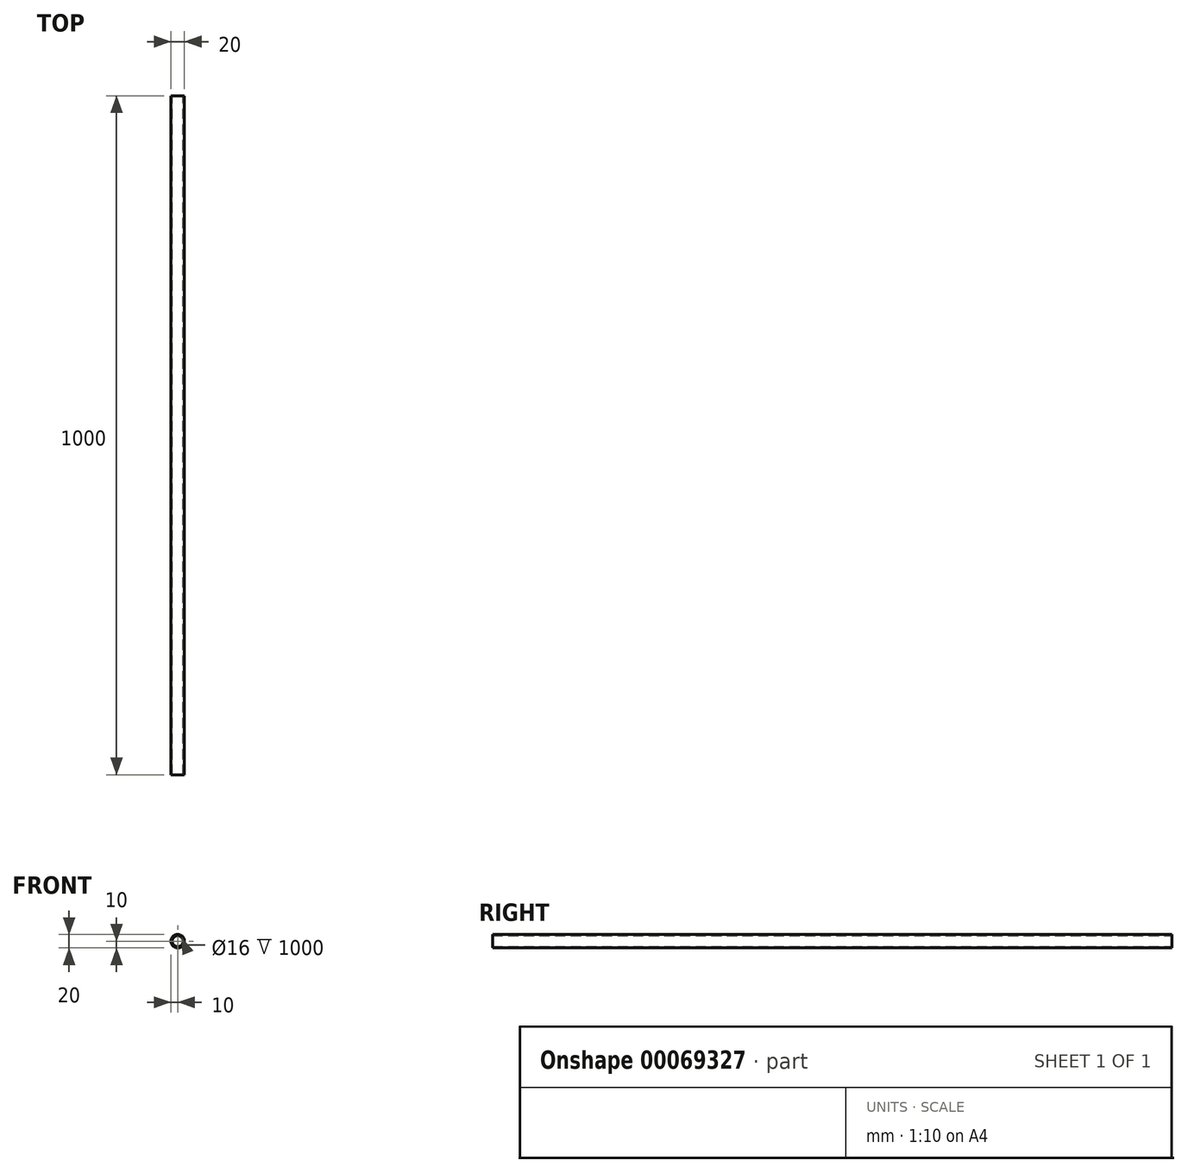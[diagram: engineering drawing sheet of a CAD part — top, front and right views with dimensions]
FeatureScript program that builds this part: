
annotation { "Feature Type Name" : "Feature", "Feature Type Description" : "" }
export const myFeature = defineFeature(function(context is Context, id is Id, definition is map)
    precondition{}
    {
        {
            var Q0;
            Q0=qCreatedBy(makeId("Front.planeOp"),FACE);
            var sketch = newSketch(context, id + "F0", { "sketchPlane" : qUnion([Q0])});
            skCircle(sketch, "E0", {"center": v(0, 0) * mm, "radius": 8 * mm});
            skCircle(sketch, "E1.0", {"center": v(0, 0) * mm, "radius": 10 * mm});
            skSolve(sketch);
        }
        {
            var Q0;
            Q0 = qSketchRegion(id + "F0", true);
            extrude(context, id + "F1", {"entities" : qUnion([Q0]), "depth" : 1000 * mm});
        }
    });
